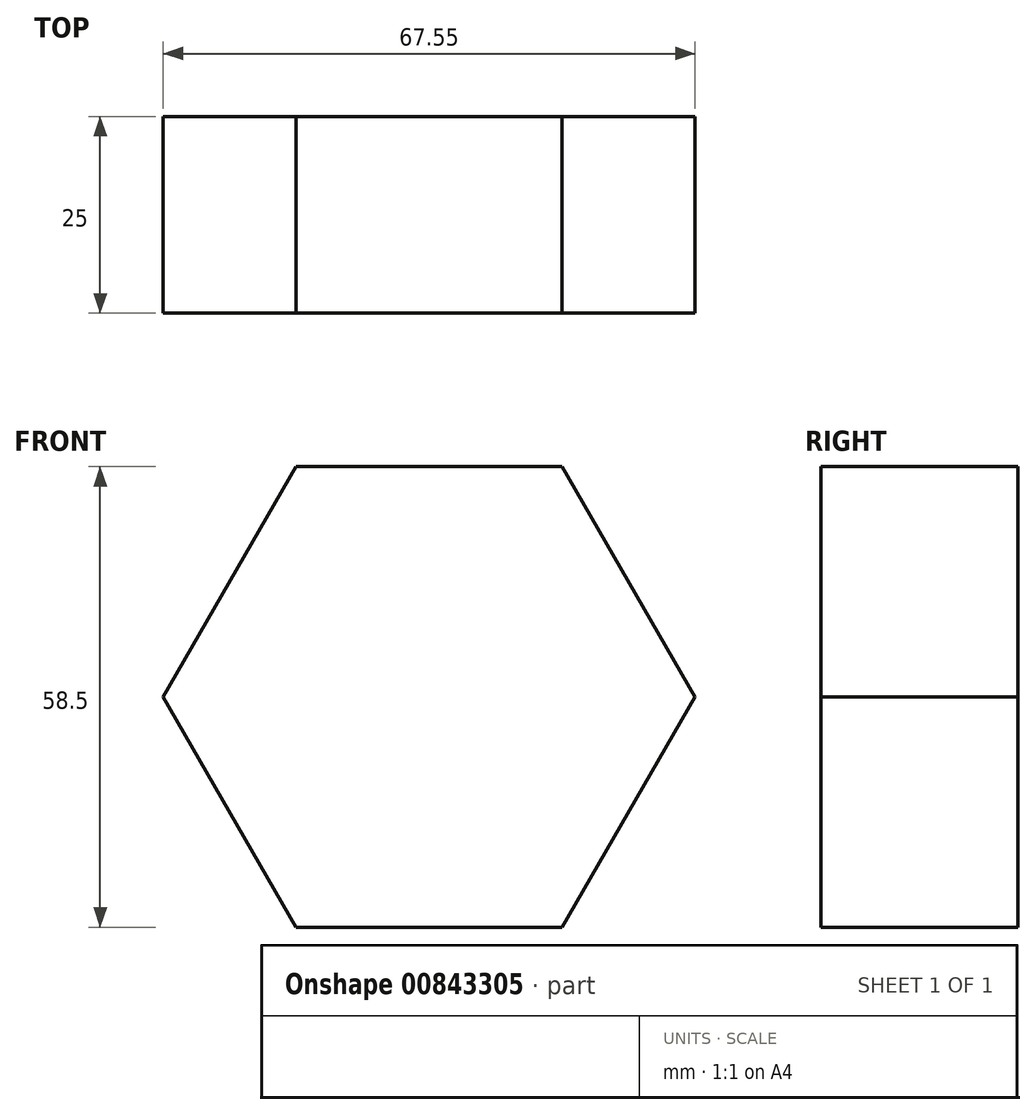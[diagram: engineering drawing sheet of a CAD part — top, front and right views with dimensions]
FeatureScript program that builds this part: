
annotation { "Feature Type Name" : "Feature", "Feature Type Description" : "" }
export const myFeature = defineFeature(function(context is Context, id is Id, definition is map)
    precondition{}
    {
        {
            var Q0;
            Q0=qCreatedBy(makeId("Front.planeOp"),FACE);
            var sketch = newSketch(context, id + "F0", { "sketchPlane" : qUnion([Q0])});
            skCircle(sketch, "E0.cCircle", {"center": v(-81.1, 0) * mm, "radius": 29.25 * mm, "construction": true});
            skLineSegment(sketch, "E0.0", {"start": v(-98, 29.25) * mm, "end": v(-64.22, 29.25) * mm});
            skLineSegment(sketch, "E0.1", {"start": v(-64.22, 29.25) * mm, "end": v(-47.33, 0) * mm});
            skLineSegment(sketch, "E0.2", {"start": v(-47.33, 0) * mm, "end": v(-64.22, -29.25) * mm});
            skLineSegment(sketch, "E0.3", {"start": v(-64.22, -29.25) * mm, "end": v(-98, -29.25) * mm});
            skLineSegment(sketch, "E0.4", {"start": v(-98, -29.25) * mm, "end": v(-114.88, 0) * mm});
            skLineSegment(sketch, "E0.5", {"start": v(-114.88, 0) * mm, "end": v(-98, 29.25) * mm});
            skPoint(sketch, "E0.0.midPoint", {"position": v(-81.1, 29.25) * mm});
            skSolve(sketch);
        }
        {
            var Q0;
            Q0=makeQuery(id+"F0.imprint","IMPRINT",FACE,{"disambiguationData":[TD([[makeQuery(id+"F0.imprint","IMPRINT",EDGE,{"derivedFrom":sQuery(id+"F0.wireOp",EDGE,"E0.0")}),-1.0]])]});
            extrude(context, id + "F1", {"entities" : qUnion([Q0]), "depth" : 25 * mm, "offsetDistance" : 25 * mm});
        }
    });
